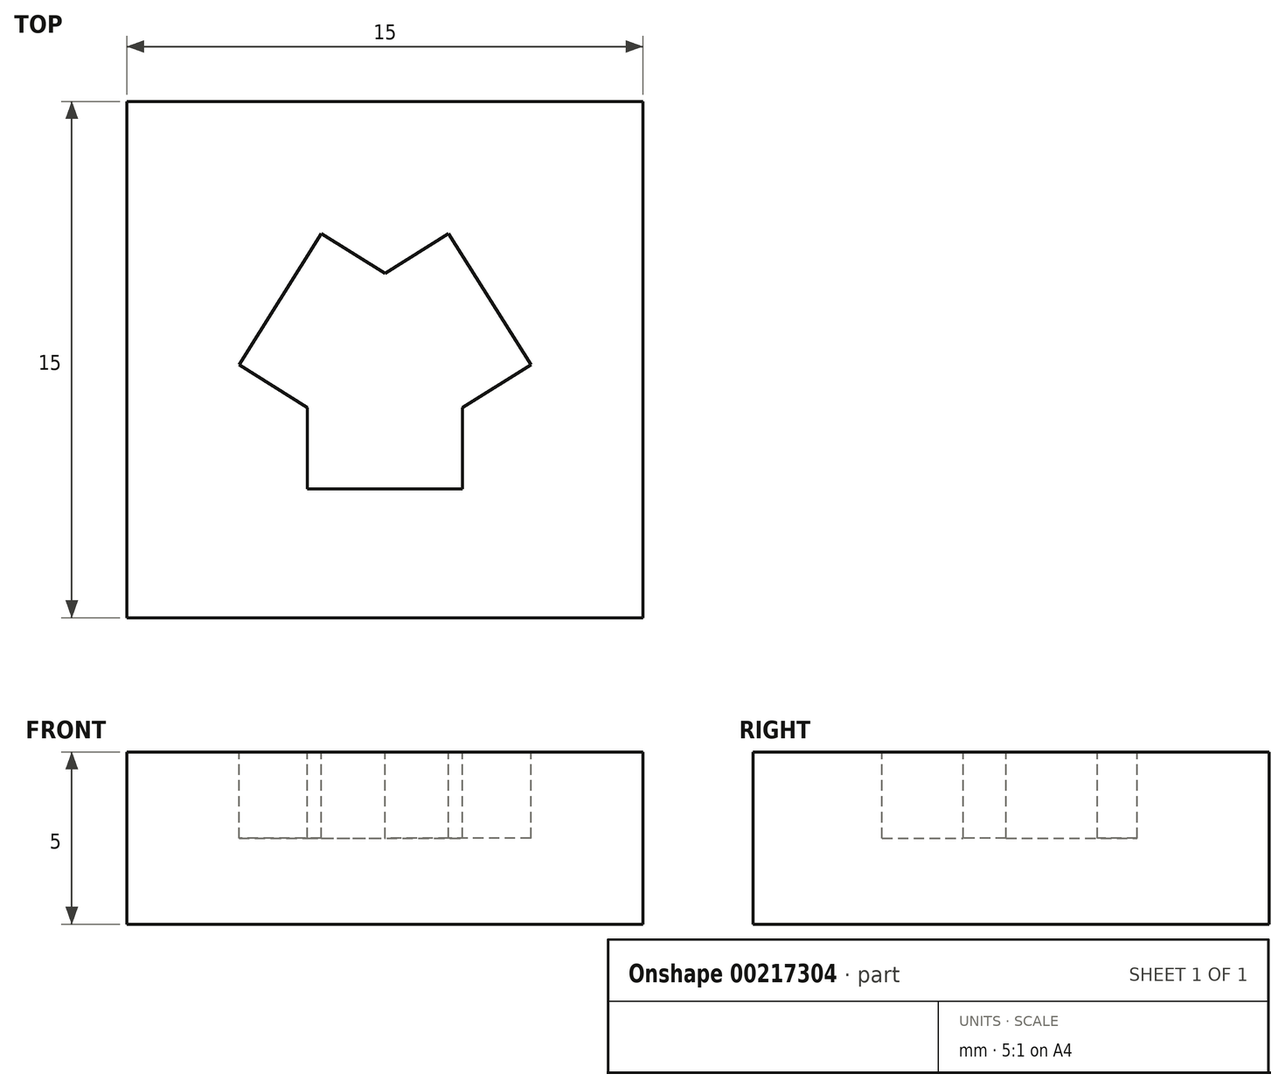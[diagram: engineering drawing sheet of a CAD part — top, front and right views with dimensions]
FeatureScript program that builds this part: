
annotation { "Feature Type Name" : "Feature", "Feature Type Description" : "" }
export const myFeature = defineFeature(function(context is Context, id is Id, definition is map)
    precondition{}
    {
        {
            var Q0;
            Q0=qCreatedBy(makeId("Top.planeOp"),FACE);
            var sketch = newSketch(context, id + "F0", { "sketchPlane" : qUnion([Q0])});
            skLineSegment(sketch, "E0.bottom", {"start": v(-7.5, 7.5) * mm, "end": v(7.5, 7.5) * mm});
            skLineSegment(sketch, "E0.top", {"start": v(-7.5, -7.5) * mm, "end": v(7.5, -7.5) * mm});
            skLineSegment(sketch, "E0.left", {"start": v(-7.5, 7.5) * mm, "end": v(-7.5, -7.5) * mm});
            skLineSegment(sketch, "E0.right", {"start": v(7.5, 7.5) * mm, "end": v(7.5, -7.5) * mm});
            skSolve(sketch);
        }
        {
            var Q0;
            Q0=makeQuery(id+"F0.imprint","IMPRINT",FACE,{"disambiguationData":[TD([[makeQuery(id+"F0.imprint","IMPRINT",EDGE,{"derivedFrom":sQuery(id+"F0.wireOp",EDGE,"E0.bottom")}),-1.0]])]});
            extrude(context, id + "F1", {"entities" : qUnion([Q0]), "depth" : 5 * mm});
        }
        {
            var Q0;
            Q0=makeQuery(id+"F1.opExtrude","CAP_FACE",FACE,{"disambiguationData":[OSD([sQuery(id+"F0.wireOp",EDGE,"E0.bottom"),sQuery(id+"F0.wireOp",EDGE,"E0.top"),sQuery(id+"F0.wireOp",EDGE,"E0.left"),sQuery(id+"F0.wireOp",EDGE,"E0.right")])],"isStart":false});
            var sketch = newSketch(context, id + "F2", { "sketchPlane" : qUnion([Q0])});
            skLineSegment(sketch, "E1", {"start": v(-1.85, 3.66) * mm, "end": v(-4.24, -0.15) * mm});
            skPoint(sketch, "E1.startSnap0", {"position": v(0, 7.5) * mm});
            skLineSegment(sketch, "E2", {"start": v(-2.25, -3.75) * mm, "end": v(2.25, -3.75) * mm});
            skLineSegment(sketch, "E3", {"start": v(4.24, -0.15) * mm, "end": v(1.85, 3.66) * mm});
            skLineSegment(sketch, "E4", {"start": v(-4.24, -0.15) * mm, "end": v(-2.25, -1.4) * mm});
            skLineSegment(sketch, "E5", {"start": v(-1.85, 3.66) * mm, "end": v(0, 2.5) * mm});
            skLineSegment(sketch, "E6", {"start": v(-2.25, -3.75) * mm, "end": v(-2.25, -1.4) * mm});
            skLineSegment(sketch, "E7", {"start": v(2.25, -3.75) * mm, "end": v(2.25, -1.4) * mm});
            skLineSegment(sketch, "E8", {"start": v(4.24, -0.15) * mm, "end": v(2.25, -1.4) * mm});
            skLineSegment(sketch, "E9", {"start": v(1.85, 3.66) * mm, "end": v(0, 2.5) * mm});
            skPoint(sketch, "E10.orphan", {"position": v(-1.5, -3.75) * mm});
            skPoint(sketch, "E11.trimOffspring.end.orphan", {"position": v(1.5, -3.75) * mm});
            skPoint(sketch, "E12.orphan", {"position": v(-6.5, -3.75) * mm});
            skPoint(sketch, "E13.orphan", {"position": v(0, 6.62) * mm});
            skPoint(sketch, "E14.orphan", {"position": v(6.5, -3.75) * mm});
            skSolve(sketch);
        }
        {
            var Q0;
            Q0=makeQuery(id+"F2.imprint","IMPRINT",FACE,{"disambiguationData":[TD([[makeQuery(id+"F2.imprint","IMPRINT",EDGE,{"derivedFrom":sQuery(id+"F2.wireOp",EDGE,"E1")}),1.0]])]});
            extrude(context, id + "F3", {"entities" : qUnion([Q0]), "operationType" : NewBodyOperationType.REMOVE, "oppositeDirection" : true, "depth" : 2.5 * mm});
        }
    });
